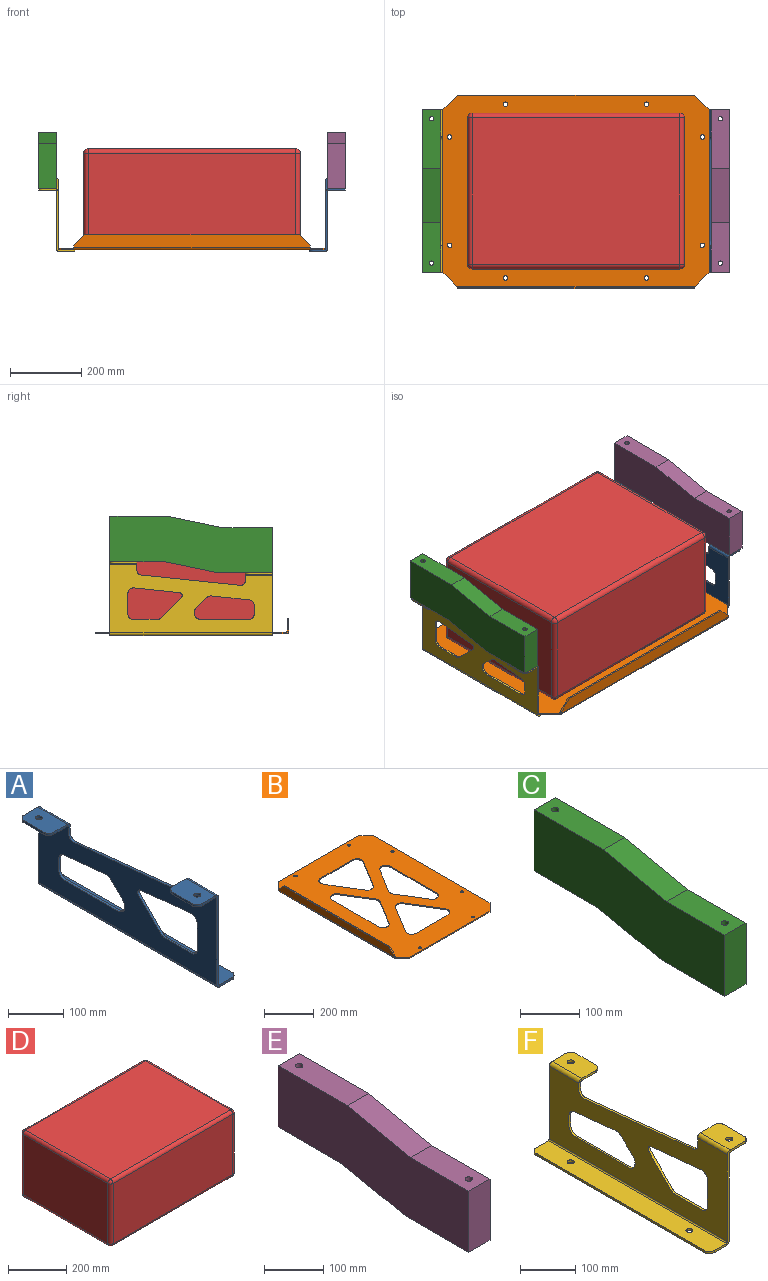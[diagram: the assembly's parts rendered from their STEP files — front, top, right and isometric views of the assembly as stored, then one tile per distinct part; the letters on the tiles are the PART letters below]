
ASSEMBLY  parts=6 mates=4
PART A: 62 faces, bbox 102x457.2x208 mm
  f0: plane 31.19x4.76mm, normal (0,-1,0), area 148.6mm2, adj f5,f6,f8,f55
  f1: plane 31.19x4.76mm, normal (0,1,0), area 148.6mm2, adj f5,f6,f7,f54
  f2: cylinder r=6.35mm len=12.7mm, axis (0,0,1), area 190mm2, adj f5,f6
  f3: cylinder r=6.35mm len=12.7mm, axis (0,0,1), area 190mm2, adj f5,f6
  f4: plane 431.8x4.76mm, normal (1,0,0), area 2056.4mm2, adj f5,f6,f7,f8
  f5: plane 457.2x43.89mm, normal (0,0,-1), area 19745.9mm2, adj f0,f1,f2,f3,f4,f7,f8,f56
  f6: plane 457.2x43.89mm, normal (0,0,1), area 19745.9mm2, adj f0,f1,f2,f3,f4,f7,f8,f57
  f7: cylinder r=12.7mm len=12.7mm, axis (0,0,-1), area 95mm2, adj f1,f4,f5,f6
  f8: cylinder r=12.7mm len=12.7mm, axis (0,0,1), area 95mm2, adj f0,f4,f5,f6
  f9: plane 35.56x4.76mm, normal (0,1,0), area 169.4mm2, adj f13,f14,f16,f58
  f10: plane 35.56x4.76mm, normal (0,-1,0), area 169.4mm2, adj f13,f14,f15,f59
  f11: cylinder r=6.35mm len=12.7mm, axis (0,0,1), area 190mm2, adj f13,f14
  f12: plane 50.8x4.76mm, normal (-1,0,0), area 241.9mm2, adj f13,f14,f15,f16
  f13: plane 76.2x48.26mm, normal (0,0,-1), area 3481.5mm2, adj f9,f10,f11,f12,f15,f16,f61
  f14: plane 76.2x48.26mm, normal (0,0,1), area 3481.5mm2, adj f9,f10,f11,f12,f15,f16,f60
  f15: cylinder r=12.7mm len=12.7mm, axis (0,0,-1), area 95mm2, adj f10,f12,f13,f14
  f16: cylinder r=12.7mm len=12.7mm, axis (0,0,1), area 95mm2, adj f9,f12,f13,f14
  f17: plane 31.08x31.08mm, normal (0,0.71,-0.71), area 209.4mm2, adj f18,f37,f38,f39
  f18: cylinder r=17.79mm len=30.38mm, axis (1,0,0), area 199.7mm2, adj f17,f19,f38,f39
  f19: plane 136.35x4.76mm, normal (0,0,1), area 649.4mm2, adj f18,f20,f38,f39
  f20: cylinder r=15.55mm len=15.55mm, axis (1,0,0), area 116.3mm2, adj f19,f21,f38,f39
  f21: plane 23.81x4.76mm, normal (0,-1,0), area 113.4mm2, adj f20,f22,f38,f39
  f22: cylinder r=15.52mm len=15.44mm, axis (1,0,0), area 108.4mm2, adj f21,f23,f38,f39
  f23: plane 106.88x11.13mm, normal (0,-0.1,-0.99), area 511.8mm2, adj f22,f37,f38,f39
  f24: plane 15.12x4.76mm, normal (0,-1,0), area 72mm2, adj f38,f39,f40,f59
  f25: plane 161.61x4.76mm, normal (0,1,0), area 769.7mm2, adj f38,f39,f54,f58
  f26: plane 193.36x4.76mm, normal (0,-1,0), area 920.9mm2, adj f38,f39,f51,f55
  f27: plane 17.76x4.76mm, normal (0,1,0), area 84.6mm2, adj f38,f39,f41,f50
  f28: cylinder r=8.31mm len=14.15mm, axis (1,0,0), area 89.2mm2, adj f29,f35,f38,f39
  f29: plane 127.86x13.32mm, normal (0,-0.1,-0.99), area 612.2mm2, adj f28,f30,f38,f39
  f30: cylinder r=15.55mm len=17.16mm, axis (1,0,0), area 124mm2, adj f29,f31,f38,f39
  f31: plane 57.59x4.76mm, normal (0,1,0), area 274.3mm2, adj f30,f32,f38,f39
  f32: cylinder r=15.55mm len=15.55mm, axis (1,0,0), area 116.3mm2, adj f31,f33,f38,f39
  f33: plane 66.91x4.76mm, normal (0,0,1), area 318.7mm2, adj f32,f34,f38,f39
  f34: cylinder r=15.55mm len=10.99mm, axis (1,0,0), area 58.2mm2, adj f33,f35,f38,f39
  f35: plane 56.58x56.58mm, normal (0,-0.71,0.71), area 381.1mm2, adj f28,f34,f38,f39
  f36: plane 279.4x29.1mm, normal (0,0.1,0.99), area 1337.8mm2, adj f38,f39,f40,f41
  f37: cylinder r=15.55mm len=12.61mm, axis (1,0,0), area 65.8mm2, adj f17,f23,f38,f39
  f38: plane 457.2x193.36mm, normal (-1,0,0), area 52473.5mm2, adj f17,f18,f19,f20,f21,f22,f23,f24
  f39: plane 457.2x193.36mm, normal (1,0,0), area 52473.5mm2, adj f17,f18,f19,f20,f21,f22,f23,f24
  f40: cylinder r=12.7mm len=14.02mm, axis (1,0,0), area 101.3mm2, adj f24,f36,f38,f39
  f41: cylinder r=12.7mm len=12.63mm, axis (1,0,0), area 88.7mm2, adj f27,f36,f38,f39
  f42: plane 35.56x4.76mm, normal (0,-1,0), area 169.4mm2, adj f46,f47,f48,f51
  f43: plane 50.8x4.76mm, normal (-1,0,0), area 241.9mm2, adj f46,f47,f48,f49
  f44: cylinder r=6.35mm len=12.7mm, axis (0,0,-1), area 190mm2, adj f46,f47
  f45: plane 35.56x4.76mm, normal (0,1,0), area 169.4mm2, adj f46,f47,f49,f50
  f46: plane 76.2x48.26mm, normal (0,0,-1), area 3481.5mm2, adj f42,f43,f44,f45,f48,f49,f53
  f47: plane 76.2x48.26mm, normal (0,0,1), area 3481.5mm2, adj f42,f43,f44,f45,f48,f49,f52
  f48: cylinder r=12.7mm len=12.7mm, axis (0,0,-1), area 95mm2, adj f42,f43,f46,f47
  f49: cylinder r=12.7mm len=12.7mm, axis (0,0,1), area 95mm2, adj f43,f45,f46,f47
  f50: plane 7.3x7.3mm, normal (0,1,0), area 36.8mm2, adj f27,f45,f52,f53
  f51: plane 7.3x7.3mm, normal (0,-1,0), area 36.8mm2, adj f26,f42,f52,f53
  f52: cylinder r=7.3mm len=76.2mm, axis (0,1,0), area 874.1mm2, adj f39,f47,f50,f51
  f53: cylinder r=2.54mm len=76.2mm, axis (0,1,0), area 304mm2, adj f38,f46,f50,f51
  f54: plane 7.3x7.3mm, normal (0,1,0), area 36.8mm2, adj f1,f25,f56,f57
  f55: plane 7.3x7.3mm, normal (0,-1,0), area 36.8mm2, adj f0,f26,f56,f57
  f56: cylinder r=7.3mm len=457.2mm, axis (0,1,0), area 5244.4mm2, adj f5,f38,f54,f55
  f57: cylinder r=2.54mm len=457.2mm, axis (0,1,0), area 1824.1mm2, adj f6,f39,f54,f55
  f58: plane 7.3x7.3mm, normal (0,1,0), area 36.8mm2, adj f9,f25,f60,f61
  f59: plane 7.3x7.3mm, normal (0,-1,0), area 36.8mm2, adj f10,f24,f60,f61
  f60: cylinder r=7.3mm len=76.2mm, axis (0,1,0), area 874.1mm2, adj f14,f39,f58,f59
  f61: cylinder r=2.54mm len=76.2mm, axis (0,1,0), area 304mm2, adj f13,f38,f58,f59
PART B: 52 faces, bbox 544.5x748.9x42.9 mm
  f0: plane 131.29x80.15mm, normal (0.85,-0.52,0), area 732.6mm2, adj f1,f38,f39,f40
  f1: cylinder r=26.09mm len=27.19mm, axis (0,0,1), area 136.2mm2, adj f0,f2,f39,f40
  f2: plane 131.29x80.15mm, normal (0.85,0.52,0), area 732.6mm2, adj f1,f3,f39,f40
  f3: cylinder r=26.09mm len=48.36mm, axis (0,0,1), area 322.3mm2, adj f2,f4,f39,f40
  f4: plane 262.58x4.76mm, normal (-1,0,0), area 1250.5mm2, adj f3,f38,f39,f40
  f5: plane 147.94x90.31mm, normal (0.85,-0.52,0), area 825.5mm2, adj f6,f37,f39,f40
  f6: cylinder r=26.09mm len=39.69mm, axis (0,0,1), area 263.3mm2, adj f5,f7,f39,f40
  f7: plane 180.63x4.76mm, normal (0,1,0), area 860.2mm2, adj f6,f8,f39,f40
  f8: cylinder r=26.09mm len=39.69mm, axis (0,0,1), area 263.3mm2, adj f7,f9,f39,f40
  f9: plane 147.94x90.31mm, normal (-0.85,-0.52,0), area 825.5mm2, adj f8,f37,f39,f40
  f10: plane 666.34x4.76mm, normal (1,0,0), area 3173.5mm2, adj f11,f28,f39,f40
  f11: plane 41.28x41.28mm, normal (0.71,-0.71,0), area 278mm2, adj f10,f12,f39,f40
  f12: plane 457.2x4.76mm, normal (0,-1,0), area 2177.4mm2, adj f11,f13,f39,f40
  f13: plane 38.74x38.74mm, normal (-0.71,-0.71,0), area 260.9mm2, adj f12,f39,f40,f49
  f14: plane 38.74x38.74mm, normal (-0.71,0.71,0), area 260.9mm2, adj f15,f39,f40,f48
  f15: plane 457.2x4.76mm, normal (0,1,0), area 2177.4mm2, adj f14,f28,f39,f40
  f16: plane 180.63x4.76mm, normal (0,-1,0), area 860.2mm2, adj f17,f27,f39,f40
  f17: cylinder r=26.09mm len=39.69mm, axis (0,0,1), area 263.3mm2, adj f16,f18,f39,f40
  f18: plane 147.94x90.31mm, normal (0.85,0.52,0), area 825.5mm2, adj f17,f19,f39,f40
  f19: cylinder r=26.09mm len=44.54mm, axis (0,0,1), area 254.2mm2, adj f18,f20,f39,f40
  f20: plane 147.94x90.31mm, normal (-0.85,0.52,0), area 825.5mm2, adj f19,f27,f39,f40
  f21: plane 262.58x4.76mm, normal (1,0,0), area 1250.5mm2, adj f22,f26,f39,f40
  f22: cylinder r=26.09mm len=48.36mm, axis (0,0,1), area 322.3mm2, adj f21,f23,f39,f40
  f23: plane 131.29x80.15mm, normal (-0.85,0.52,0), area 732.6mm2, adj f22,f24,f39,f40
  f24: cylinder r=26.09mm len=27.19mm, axis (0,0,1), area 136.2mm2, adj f23,f25,f39,f40
  f25: plane 131.29x80.15mm, normal (-0.85,-0.52,0), area 732.6mm2, adj f24,f26,f39,f40
  f26: cylinder r=26.09mm len=48.36mm, axis (0,0,1), area 322.3mm2, adj f21,f25,f39,f40
  f27: cylinder r=26.09mm len=39.69mm, axis (0,0,1), area 263.3mm2, adj f16,f20,f39,f40
  f28: plane 41.28x41.28mm, normal (0.71,0.71,0), area 278mm2, adj f10,f15,f39,f40
  f29: cylinder r=6.35mm len=12.7mm, axis (0,0,1), area 190mm2, adj f39,f40
  f30: cylinder r=6.35mm len=12.7mm, axis (0,0,1), area 190mm2, adj f39,f40
  f31: cylinder r=6.35mm len=12.7mm, axis (0,0,1), area 190mm2, adj f39,f40
  f32: cylinder r=6.35mm len=12.7mm, axis (0,0,1), area 190mm2, adj f39,f40
  f33: cylinder r=6.35mm len=12.7mm, axis (0,0,1), area 190mm2, adj f39,f40
  f34: cylinder r=6.35mm len=12.7mm, axis (0,0,1), area 190mm2, adj f39,f40
  f35: cylinder r=6.35mm len=12.7mm, axis (0,0,1), area 190mm2, adj f39,f40
  f36: cylinder r=6.35mm len=12.7mm, axis (0,0,1), area 190mm2, adj f39,f40
  f37: cylinder r=26.09mm len=44.54mm, axis (0,0,1), area 254.2mm2, adj f5,f9,f39,f40
  f38: cylinder r=26.09mm len=48.36mm, axis (0,0,1), area 322.3mm2, adj f0,f4,f39,f40
  f39: plane 748.89x537.21mm, normal (0,0,-1), area 284501.3mm2, adj f0,f1,f2,f3,f4,f5,f6,f7
  f40: plane 748.89x537.21mm, normal (0,0,1), area 284501.3mm2, adj f0,f1,f2,f3,f4,f5,f6,f7
  f41: plane 4.76x3.81mm, normal (0,-1,0), area 18.1mm2, adj f44,f45,f46,f49
  f42: plane 602.84x4.76mm, normal (0,0,1), area 2871mm2, adj f44,f45,f46,f47
  f43: plane 4.76x3.81mm, normal (0,1,0), area 18.1mm2, adj f44,f45,f47,f48
  f44: plane 666.34x35.56mm, normal (-1,0,0), area 22687.1mm2, adj f41,f42,f43,f46,f47,f50
  f45: plane 666.34x35.56mm, normal (1,0,0), area 22687.1mm2, adj f41,f42,f43,f46,f47,f51
  f46: plane 31.75x31.75mm, normal (0,-0.71,0.71), area 213.8mm2, adj f41,f42,f44,f45
  f47: plane 31.75x31.75mm, normal (0,0.71,0.71), area 213.8mm2, adj f42,f43,f44,f45
  f48: bspline ~7.3x7.3mm, area 41.5mm2, adj f14,f43,f50,f51
  f49: bspline ~7.3x7.3mm, area 41.6mm2, adj f13,f41,f50,f51
  f50: cylinder r=7.3mm len=671.42mm, axis (0,1,0), area 7651.9mm2, adj f39,f44,f48,f49
  f51: cylinder r=2.54mm len=671.42mm, axis (0,1,0), area 2661.5mm2, adj f40,f45,f48,f49
PART C: 12 faces, bbox 50.8x457.2x158.8 mm
  f0: plane 457.2x158.75mm, normal (-1,0,0), area 58480mm2, adj f1,f3,f4,f5,f6,f7,f8,f9
  f1: plane 152.4x50.8mm, normal (0,0,-1), area 7615.2mm2, adj f0,f2,f3,f9,f11
  f2: plane 457.2x158.75mm, normal (1,0,0), area 58480mm2, adj f1,f3,f4,f5,f6,f7,f8,f9
  f3: plane 127x50.8mm, normal (0,-1,0), area 6451.6mm2, adj f0,f1,f2,f6
  f4: plane 127x50.8mm, normal (0,1,0), area 6451.6mm2, adj f0,f2,f5,f8
  f5: plane 165.49x50.8mm, normal (0,0,1), area 8280.1mm2, adj f0,f2,f4,f7,f10
  f6: plane 139.31x50.8mm, normal (0,0,1), area 6950.3mm2, adj f0,f2,f3,f7,f11
  f7: plane 152.4x50.8mm, normal (0,-0.2,0.98), area 7908.1mm2, adj f0,f2,f5,f6
  f8: plane 152.4x50.8mm, normal (0,0,-1), area 7615.2mm2, adj f0,f2,f4,f9,f10
  f9: plane 152.4x50.8mm, normal (0,0.2,-0.98), area 7908.1mm2, adj f0,f1,f2,f8
  f10: cylinder r=6.35mm len=127mm, axis (0,0,1), area 5067.1mm2, adj f5,f8
  f11: cylinder r=6.35mm len=127mm, axis (0,0,1), area 5067.1mm2, adj f1,f6
PART D: 26 faces, bbox 609.6x438.2x279.4 mm
  f0: plane 412.75x254mm, normal (-1,0,0), area 104838.5mm2, adj f14,f19,f22,f25
  f1: plane 584.2x254mm, normal (0,-1,0), area 148386.8mm2, adj f11,f20,f21,f25
  f2: plane 412.75x254mm, normal (1,0,0), area 104838.5mm2, adj f6,f10,f11,f12
  f3: plane 584.2x254mm, normal (0,1,0), area 148386.8mm2, adj f6,f9,f13,f14
  f4: plane 584.2x412.75mm, normal (0,0,1), area 241128.6mm2, adj f9,f10,f19,f20
  f5: plane 584.2x412.75mm, normal (0,0,-1), area 241128.6mm2, adj f12,f13,f21,f22
  f6: cylinder r=12.7mm len=254mm, axis (0,0,1), area 5067.1mm2, adj f2,f3,f7,f8
  f7: sphere r=12.7mm, area 253.4mm2, adj f6,f9,f10
  f8: sphere r=12.7mm, area 253.4mm2, adj f6,f12,f13
  f9: cylinder r=12.7mm len=584.2mm, axis (1,0,0), area 11654.3mm2, adj f3,f4,f7,f15
  f10: cylinder r=12.7mm len=412.75mm, axis (0,-1,0), area 8234mm2, adj f2,f4,f7,f16
  f11: cylinder r=12.7mm len=254mm, axis (0,0,-1), area 5067.1mm2, adj f1,f2,f16,f17
  f12: cylinder r=12.7mm len=412.75mm, axis (0,1,0), area 8234mm2, adj f2,f5,f8,f17
  f13: cylinder r=12.7mm len=584.2mm, axis (-1,0,0), area 11654.3mm2, adj f3,f5,f8,f18
  f14: cylinder r=12.7mm len=254mm, axis (0,0,-1), area 5067.1mm2, adj f0,f3,f15,f18
  f15: sphere r=12.7mm, area 253.4mm2, adj f9,f14,f19
  f16: sphere r=12.7mm, area 253.4mm2, adj f10,f11,f20
  f17: sphere r=12.7mm, area 253.4mm2, adj f11,f12,f21
  f18: sphere r=12.7mm, area 253.4mm2, adj f13,f14,f22
  f19: cylinder r=12.7mm len=412.75mm, axis (0,1,0), area 8234mm2, adj f0,f4,f15,f23
  f20: cylinder r=12.7mm len=584.2mm, axis (-1,0,0), area 11654.3mm2, adj f1,f4,f16,f23
  f21: cylinder r=12.7mm len=584.2mm, axis (1,0,0), area 11654.3mm2, adj f1,f5,f17,f24
  f22: cylinder r=12.7mm len=412.75mm, axis (0,-1,0), area 8234mm2, adj f0,f5,f18,f24
  f23: sphere r=12.7mm, area 253.4mm2, adj f19,f20,f25
  f24: sphere r=12.7mm, area 253.4mm2, adj f21,f22,f25
  f25: cylinder r=12.7mm len=254mm, axis (0,0,1), area 5067.1mm2, adj f0,f1,f23,f24
PART E: 12 faces, bbox 50.8x457.2x158.8 mm
  f0: plane 152.4x50.8mm, normal (0,0,-1), area 7615.2mm2, adj f1,f2,f3,f9,f11
  f1: plane 127x50.8mm, normal (0,-1,0), area 6451.6mm2, adj f0,f2,f3,f7
  f2: plane 457.2x158.75mm, normal (-1,0,0), area 58480mm2, adj f0,f1,f4,f5,f6,f7,f8,f9
  f3: plane 457.2x158.75mm, normal (1,0,0), area 58480mm2, adj f0,f1,f4,f5,f6,f7,f8,f9
  f4: plane 127x50.8mm, normal (0,1,0), area 6451.6mm2, adj f2,f3,f5,f8
  f5: plane 165.49x50.8mm, normal (0,0,1), area 8280.1mm2, adj f2,f3,f4,f6,f10
  f6: plane 152.4x50.8mm, normal (0,-0.2,0.98), area 7908.1mm2, adj f2,f3,f5,f7
  f7: plane 139.31x50.8mm, normal (0,0,1), area 6950.3mm2, adj f1,f2,f3,f6,f11
  f8: plane 152.4x50.8mm, normal (0,0,-1), area 7615.2mm2, adj f2,f3,f4,f9,f10
  f9: plane 152.4x50.8mm, normal (0,0.2,-0.98), area 7908.1mm2, adj f0,f2,f3,f8
  f10: cylinder r=6.35mm len=127mm, axis (0,0,1), area 5067.1mm2, adj f5,f8
  f11: cylinder r=6.35mm len=127mm, axis (0,0,1), area 5067.1mm2, adj f0,f7
PART F: 62 faces, bbox 102x457.2x208 mm
  f0: plane 31.19x4.76mm, normal (0,-1,0), area 148.6mm2, adj f5,f6,f8,f55
  f1: plane 431.8x4.76mm, normal (-1,0,0), area 2056.4mm2, adj f5,f6,f7,f8
  f2: plane 31.19x4.76mm, normal (0,1,0), area 148.6mm2, adj f5,f6,f7,f54
  f3: cylinder r=6.35mm len=12.7mm, axis (0,0,1), area 190mm2, adj f5,f6
  f4: cylinder r=6.35mm len=12.7mm, axis (0,0,1), area 190mm2, adj f5,f6
  f5: plane 457.2x43.89mm, normal (0,0,-1), area 19745.9mm2, adj f0,f1,f2,f3,f4,f7,f8,f56
  f6: plane 457.2x43.89mm, normal (0,0,1), area 19745.9mm2, adj f0,f1,f2,f3,f4,f7,f8,f57
  f7: cylinder r=12.7mm len=12.7mm, axis (0,0,-1), area 95mm2, adj f1,f2,f5,f6
  f8: cylinder r=12.7mm len=12.7mm, axis (0,0,1), area 95mm2, adj f0,f1,f5,f6
  f9: plane 35.56x4.76mm, normal (0,1,0), area 169.4mm2, adj f13,f14,f16,f58
  f10: plane 50.8x4.76mm, normal (1,0,0), area 241.9mm2, adj f13,f14,f15,f16
  f11: plane 35.56x4.76mm, normal (0,-1,0), area 169.4mm2, adj f13,f14,f15,f59
  f12: cylinder r=6.35mm len=12.7mm, axis (0,0,1), area 190mm2, adj f13,f14
  f13: plane 76.2x48.26mm, normal (0,0,-1), area 3481.5mm2, adj f9,f10,f11,f12,f15,f16,f61
  f14: plane 76.2x48.26mm, normal (0,0,1), area 3481.5mm2, adj f9,f10,f11,f12,f15,f16,f60
  f15: cylinder r=12.7mm len=12.7mm, axis (0,0,-1), area 95mm2, adj f10,f11,f13,f14
  f16: cylinder r=12.7mm len=12.7mm, axis (0,0,1), area 95mm2, adj f9,f10,f13,f14
  f17: plane 23.81x4.76mm, normal (0,-1,0), area 113.4mm2, adj f18,f37,f38,f39
  f18: cylinder r=15.55mm len=15.55mm, axis (-1,0,0), area 116.3mm2, adj f17,f19,f38,f39
  f19: plane 136.35x4.76mm, normal (0,0,1), area 649.4mm2, adj f18,f20,f38,f39
  f20: cylinder r=17.79mm len=30.38mm, axis (-1,0,0), area 199.7mm2, adj f19,f21,f38,f39
  f21: plane 31.08x31.08mm, normal (0,0.71,-0.71), area 209.4mm2, adj f20,f22,f38,f39
  f22: cylinder r=15.55mm len=12.61mm, axis (-1,0,0), area 65.8mm2, adj f21,f23,f38,f39
  f23: plane 106.88x11.13mm, normal (0,-0.1,-0.99), area 511.8mm2, adj f22,f37,f38,f39
  f24: plane 193.36x4.76mm, normal (0,-1,0), area 920.9mm2, adj f38,f39,f51,f55
  f25: plane 161.61x4.76mm, normal (0,1,0), area 769.7mm2, adj f38,f39,f54,f58
  f26: plane 15.12x4.76mm, normal (0,-1,0), area 72mm2, adj f38,f39,f41,f59
  f27: plane 279.4x29.1mm, normal (0,0.1,0.99), area 1337.8mm2, adj f38,f39,f40,f41
  f28: plane 17.76x4.76mm, normal (0,1,0), area 84.6mm2, adj f38,f39,f40,f50
  f29: cylinder r=15.55mm len=15.55mm, axis (-1,0,0), area 116.3mm2, adj f30,f36,f38,f39
  f30: plane 57.59x4.76mm, normal (0,1,0), area 274.3mm2, adj f29,f31,f38,f39
  f31: cylinder r=15.55mm len=17.16mm, axis (-1,0,0), area 124mm2, adj f30,f32,f38,f39
  f32: plane 127.86x13.32mm, normal (0,-0.1,-0.99), area 612.2mm2, adj f31,f33,f38,f39
  f33: cylinder r=8.31mm len=14.15mm, axis (-1,0,0), area 89.2mm2, adj f32,f34,f38,f39
  f34: plane 56.58x56.58mm, normal (0,-0.71,0.71), area 381.1mm2, adj f33,f35,f38,f39
  f35: cylinder r=15.55mm len=10.99mm, axis (-1,0,0), area 58.2mm2, adj f34,f36,f38,f39
  f36: plane 66.91x4.76mm, normal (0,0,1), area 318.7mm2, adj f29,f35,f38,f39
  f37: cylinder r=15.52mm len=15.44mm, axis (-1,0,0), area 108.4mm2, adj f17,f23,f38,f39
  f38: plane 457.2x193.36mm, normal (1,0,0), area 52473.5mm2, adj f17,f18,f19,f20,f21,f22,f23,f24
  f39: plane 457.2x193.36mm, normal (-1,0,0), area 52473.5mm2, adj f17,f18,f19,f20,f21,f22,f23,f24
  f40: cylinder r=12.7mm len=12.63mm, axis (-1,0,0), area 88.7mm2, adj f27,f28,f38,f39
  f41: cylinder r=12.7mm len=14.02mm, axis (-1,0,0), area 101.3mm2, adj f26,f27,f38,f39
  f42: plane 35.56x4.76mm, normal (0,1,0), area 169.4mm2, adj f46,f47,f49,f50
  f43: plane 50.8x4.76mm, normal (1,0,0), area 241.9mm2, adj f46,f47,f48,f49
  f44: cylinder r=6.35mm len=12.7mm, axis (0,0,-1), area 190mm2, adj f46,f47
  f45: plane 35.56x4.76mm, normal (0,-1,0), area 169.4mm2, adj f46,f47,f48,f51
  f46: plane 76.2x48.26mm, normal (0,0,-1), area 3481.5mm2, adj f42,f43,f44,f45,f48,f49,f53
  f47: plane 76.2x48.26mm, normal (0,0,1), area 3481.5mm2, adj f42,f43,f44,f45,f48,f49,f52
  f48: cylinder r=12.7mm len=12.7mm, axis (0,0,-1), area 95mm2, adj f43,f45,f46,f47
  f49: cylinder r=12.7mm len=12.7mm, axis (0,0,1), area 95mm2, adj f42,f43,f46,f47
  f50: plane 7.3x7.3mm, normal (0,1,0), area 36.8mm2, adj f28,f42,f52,f53
  f51: plane 7.3x7.3mm, normal (0,-1,0), area 36.8mm2, adj f24,f45,f52,f53
  f52: cylinder r=7.3mm len=76.2mm, axis (0,1,0), area 874.1mm2, adj f39,f47,f50,f51
  f53: cylinder r=2.54mm len=76.2mm, axis (0,1,0), area 304mm2, adj f38,f46,f50,f51
  f54: plane 7.3x7.3mm, normal (0,1,0), area 36.8mm2, adj f2,f25,f56,f57
  f55: plane 7.3x7.3mm, normal (0,-1,0), area 36.8mm2, adj f0,f24,f56,f57
  f56: cylinder r=7.3mm len=457.2mm, axis (0,1,0), area 5244.4mm2, adj f5,f38,f54,f55
  f57: cylinder r=2.54mm len=457.2mm, axis (0,1,0), area 1824.1mm2, adj f6,f39,f54,f55
  f58: plane 7.3x7.3mm, normal (0,1,0), area 36.8mm2, adj f9,f25,f60,f61
  f59: plane 7.3x7.3mm, normal (0,-1,0), area 36.8mm2, adj f11,f26,f60,f61
  f60: cylinder r=7.3mm len=76.2mm, axis (0,1,0), area 874.1mm2, adj f14,f39,f58,f59
  f61: cylinder r=2.54mm len=76.2mm, axis (0,1,0), area 304mm2, adj f13,f38,f58,f59
PLACE A rot(axis=(0,0,1),180deg) t=(-236.51,-172.98,-353.66)mm
PLACE B rot(axis=(0,0,1),90deg) t=(569.38,-214.25,-344.14)mm
PLACE C t=(-236.87,284.22,-177.45)mm fixed
PLACE D t=(-110.07,-163.45,-344.14)mm
PLACE E t=(-236.87,284.22,-177.45)mm fixed
PLACE F rot(axis=(0,0,1),180deg) t=(-134.88,-172.98,-353.66)mm
MATE fastened D.f5 <-> B.f40  axis (0,0,-1) through (486.83,55.62,-344.14)mm
MATE fastened F.f44 <-> C.f10  axis (0,0,1) through (-211.47,258.82,-145.7)mm
MATE fastened B.f31 <-> A.f2  axis (0,0,-1) through (550.33,208.02,-348.9)mm
MATE fastened A.f44 <-> E.f10  axis (0,0,1) through (601.33,258.82,-145.7)mm
